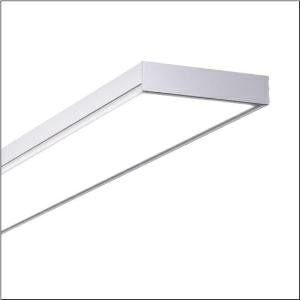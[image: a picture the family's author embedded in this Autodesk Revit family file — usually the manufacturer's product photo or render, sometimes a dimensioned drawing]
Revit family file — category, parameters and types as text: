
# Revit family: apollon_r__31_surface_51mp25wm2441e_2def
name_source: partatom
category: Lighting Fixtures
units: mm (PartAtom-declared; Revit-internal decimal feet)

## family parameters
Cut with Voids When Loaded = No
Host = Face
Light Source = No
Part Type = Normal
Room Calculation Point = No
Round Connector Dimension = Use Diameter
Shared = No

## types (1)
- Apollon® 31 Surface (1 x LED, 3800 lm, 27 W, 4000K)
    Apparent Load = 27 VA
    CIE Flux Codes = 61 87 97 97 100
    Color Rendering = 80
    Color Temperature = 4000K
    Default Elevation = 1800 mm
    Description = Apollon® 31 Surface, office luminaire, primary optical cover: micro prismatic cover, of PMMA, light emission: direct distribution, primary light characteristic: symmetric, installation type: surface-mounted, LED, rated luminous flux: 3.800lm, luminous efficacy: 139lm/W, light colour: 840, colour temperature: 4000K, control gear: ECG Multilumen, with terminal, 3-pole, mains connection: 220..240V, AC, 50/60Hz, rated input power: 27W, housing, of sheet steel, coil coated, metallic grey (RAL 9006), length: 1.245mm, width: 200mm, height: 44mm, protection rating (complete): IP20, insulation class (complete): insulation class II (safety insulation), certification: CE, impact resistance: IK02, permissible operating ambient temperature: -20..+40°C, packaging unit: 1 piece
    Height = 44 mm
    Lamp = 1 x LED
    Lamp Light Flux = 3800 lm
    Lamp Power = 27 W
    Lamp count = 1
    Length = 1245 mm
    Luminous efficacy = 141 lm/W
    Manufacturer = Siteco
    ModVariant = No
    Model = 51MP25WM2441E
    Mounting Place = Ceiling
    Mounting Type = Surface mounted
    Number of Poles = 1
    OnlyDefault = Yes
    Power Factor = 1
    Product Name = Apollon® 31 Surface
    Product group = office luminaire | ceiling mounted
    ProductGroupID = 304
    Protection Class = Protection class II
    Protection Degree = IP 20
    RLX_Detail_Level = 1
    RLX_Emergency_Light_Flux = 0 lm
    RLX_Emergency_Type = 0
    RLX_Emergency_Type_DB = No
    RlxData = <blob elided: 24097 chars, md5=44d552ee>
    Socket = socket
    Standby Power = 0 W
    System Light Flux = 3800 lm
    System Power = 27 W
    Type Comments = Product without accessories
    Type Image = l_1007091.jpg
    URL = http://relux.com
    VarID = ---
    Voltage = 0 V
    Weight = 0.00 kg
    Width = 200 mm  [stored 0.656168 ft]

note: [stored X ft] marks values corroborated as IEEE doubles in the binary element streams (Revit-internal decimal feet)

## geometry (parser evidence)
native form markers: Blend x4, Sweep x10
no freeform markers — native parametric forms only
